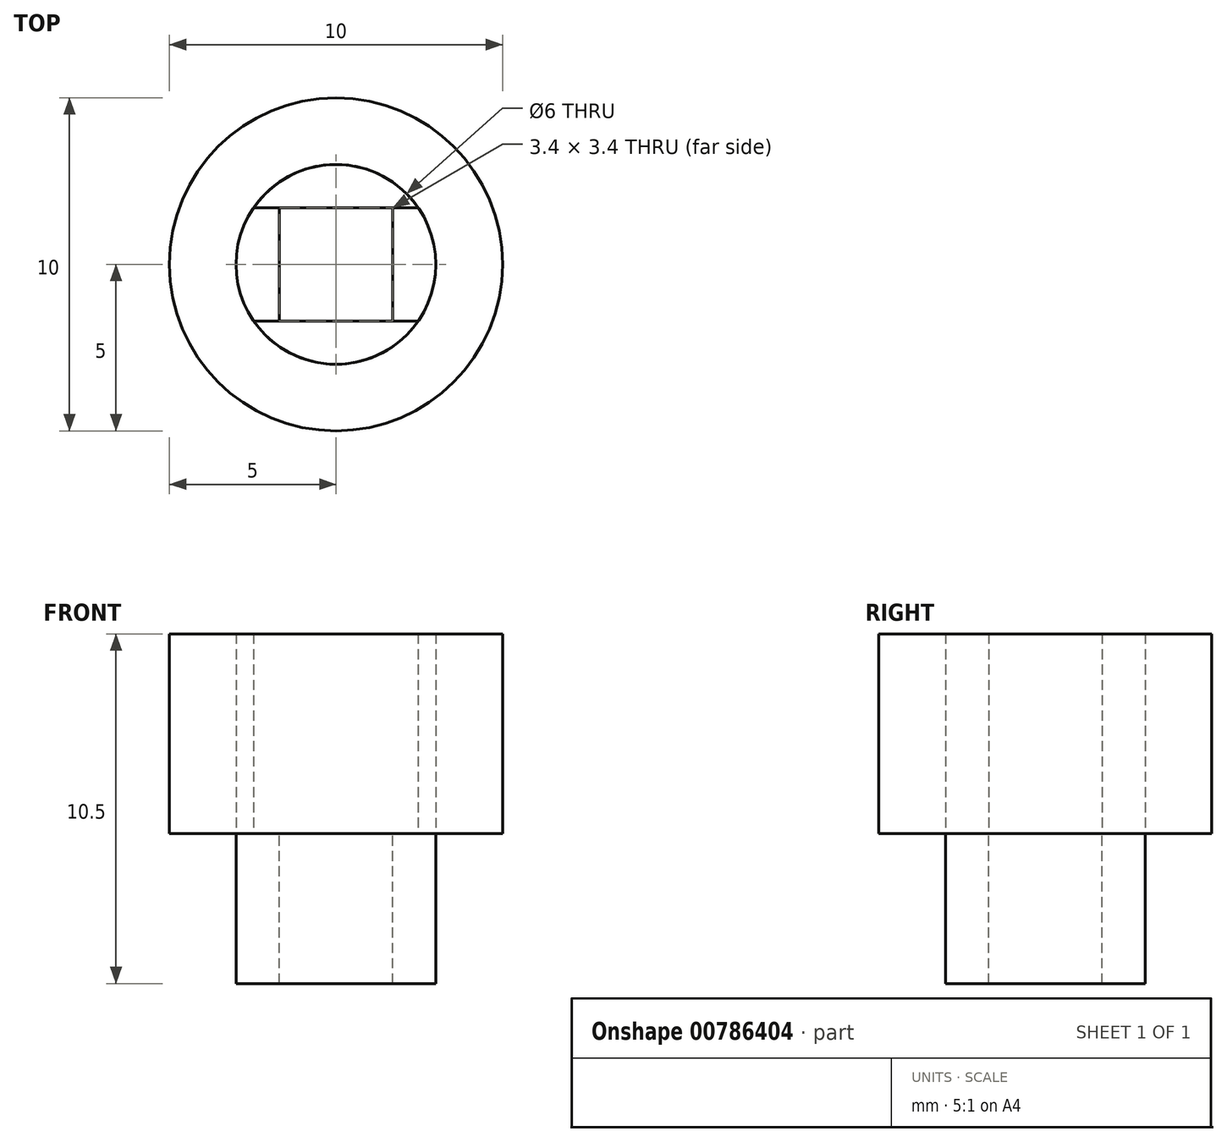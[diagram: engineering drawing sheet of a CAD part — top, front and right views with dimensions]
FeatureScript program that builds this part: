
annotation { "Feature Type Name" : "Feature", "Feature Type Description" : "" }
export const myFeature = defineFeature(function(context is Context, id is Id, definition is map)
    precondition{}
    {
        {
            var Q0;
            Q0=qCreatedBy(makeId("Top.planeOp"),FACE);
            var sketch = newSketch(context, id + "F0", { "sketchPlane" : qUnion([Q0])});
            skCircle(sketch, "E0", {"center": v(0, 0) * mm, "radius": 5 * mm});
            skCircle(sketch, "E1", {"center": v(0, 0) * mm, "radius": 3 * mm});
            skLineSegment(sketch, "E2.bottom", {"start": v(-1.7, 1.7) * mm, "end": v(1.7, 1.7) * mm});
            skLineSegment(sketch, "E2.top", {"start": v(-1.7, -1.7) * mm, "end": v(1.7, -1.7) * mm});
            skLineSegment(sketch, "E2.left", {"start": v(-1.7, 1.7) * mm, "end": v(-1.7, -1.7) * mm});
            skLineSegment(sketch, "E2.right", {"start": v(1.7, 1.7) * mm, "end": v(1.7, -1.7) * mm});
            skLineSegment(sketch, "E3.bottom", {"start": v(-2.47, 1.7) * mm, "end": v(2.47, 1.7) * mm});
            skLineSegment(sketch, "E3.top", {"start": v(-2.47, -1.7) * mm, "end": v(2.47, -1.7) * mm});
            skPoint(sketch, "E4.orphan", {"position": v(-3, 1.7) * mm});
            skPoint(sketch, "E3.left.end.orphan", {"position": v(-3, -1.7) * mm});
            skSolve(sketch);
        }
        {
            var Q0;
            Q0=makeQuery(id+"F0.imprint","IMPRINT",FACE,{"disambiguationData":[TD([[makeQuery(id+"F0.imprint","IMPRINT",EDGE,{"derivedFrom":sQuery(id+"F0.wireOp",EDGE,"E1")}),1.0]])]});
            extrude(context, id + "F1", {"entities" : qUnion([Q0]), "depth" : -4.5 * mm, "offsetDistance" : 25 * mm});
        }
        {
            var Q0;
            Q0=makeQuery(id+"F0.imprint","IMPRINT",FACE,{"disambiguationData":[TD([[makeQuery(id+"F0.imprint","IMPRINT",EDGE,{"derivedFrom":sQuery(id+"F0.wireOp",EDGE,"E0")}),1.0]])]});
            extrude(context, id + "F2", {"entities" : qUnion([Q0]), "depth" : 6 * mm, "offsetDistance" : 25 * mm});
        }
        {
            var Q0;
            {var subQ0=sQuery(id+"F0.wireOp",EDGE,"E3.bottom");var subQ1=sQuery(id+"F0.wireOp",EDGE,"E1");var subQ2=makeQuery(id+"F0.imprint","INTERSECT",VERTEX,{"disambiguationData":[OD(0.0)],"derivedFrom":[subQ1,subQ0]});Q0=makeQuery(id+"F0.imprint","IMPRINT",FACE,{"disambiguationData":[TD([[makeQuery(id+"F0.imprint","IMPRINT",EDGE,{"disambiguationData":[TD([[subQ2,1.0]])],"derivedFrom":subQ1}),1.0]])]});}
            extrude(context, id + "F3", {"entities" : qUnion([Q0]), "depth" : 6 * mm, "offsetDistance" : 25 * mm});
        }
        {
            var Q0;
            {var subQ0=sQuery(id+"F0.wireOp",EDGE,"E3.top");var subQ1=sQuery(id+"F0.wireOp",EDGE,"E1");var subQ2=makeQuery(id+"F0.imprint","INTERSECT",VERTEX,{"disambiguationData":[OD(0.0)],"derivedFrom":[subQ1,subQ0]});Q0=makeQuery(id+"F0.imprint","IMPRINT",FACE,{"disambiguationData":[TD([[makeQuery(id+"F0.imprint","IMPRINT",EDGE,{"disambiguationData":[TD([[subQ2,-1.0]])],"derivedFrom":subQ1}),1.0]])]});}
            extrude(context, id + "F4", {"entities" : qUnion([Q0]), "depth" : 6 * mm, "offsetDistance" : 25 * mm});
        }
    });
